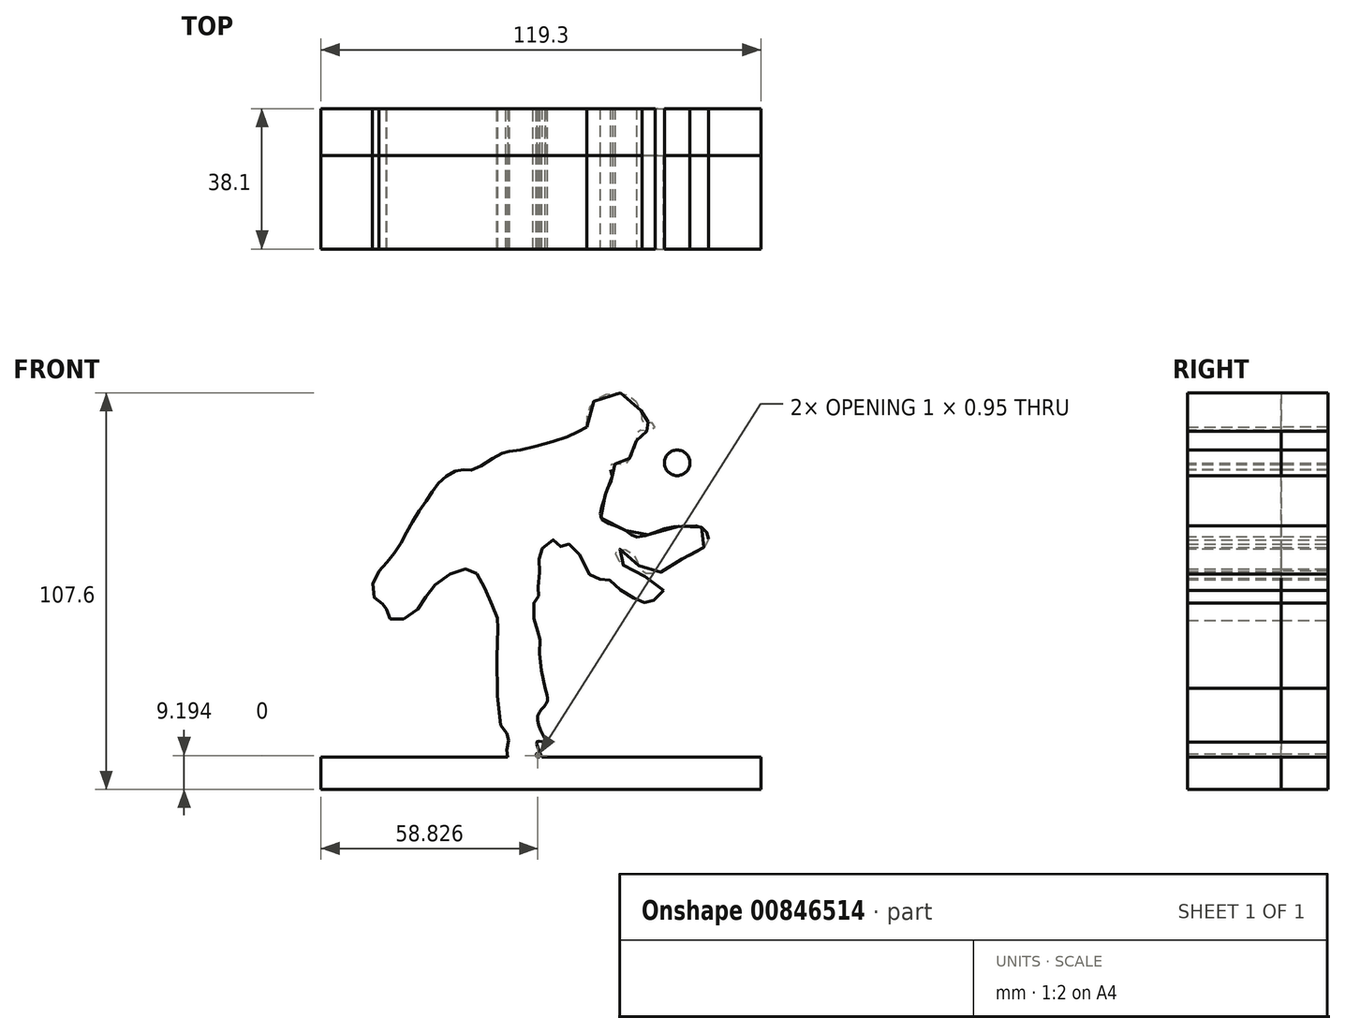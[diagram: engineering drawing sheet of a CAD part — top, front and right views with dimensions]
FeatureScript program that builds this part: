
annotation { "Feature Type Name" : "Feature", "Feature Type Description" : "" }
export const myFeature = defineFeature(function(context is Context, id is Id, definition is map)
    precondition{}
    {
        {
            var Q0;
            Q0=qCreatedBy(makeId("Front.planeOp"),FACE);
            var sketch = newSketch(context, id + "F0", { "sketchPlane" : qUnion([Q0])});
            skFitSpline(sketch, "E0", {"points": [v(-37.44, 0) * mm, v(-32.4, 6.14) * mm, v(-28.41, 13.3) * mm, v(-23.9, 20.2) * mm, v(-20.05, 25.12) * mm, v(-15.28, 27.5) * mm, v(-11.96, 27.5) * mm, v(-4.66, 31.75) * mm, v(-1.08, 32.55) * mm, v(12.46, 36) * mm, v(18.93, 39.1) * mm], "startDerivative": vector(50.52, 55.27) * mm, "endDerivative": vector(52.32, 30.3) * mm});
            skFitSpline(sketch, "E1", {"points": [v(18.93, 39.1) * mm, v(20.04, 45.09) * mm, v(25.4, 48.21) * mm, v(31.53, 46.87) * mm, v(33.88, 41.74) * mm, v(33.77, 40.62) * mm, v(37.11, 40.07) * mm, v(36.67, 38.06) * mm, v(32.87, 38.17) * mm, v(32.43, 36.05) * mm, v(31.65, 32.48) * mm, v(30.3, 30.25) * mm, v(29.08, 28.8) * mm, v(25.95, 29.13) * mm, v(25.28, 28.35) * mm, v(25.84, 25.34) * mm, v(24.62, 22.66) * mm, v(23.28, 18.2) * mm, v(22.83, 14.29) * mm, v(28.86, 11.39) * mm, v(32.43, 9.27) * mm, v(40.35, 11.61) * mm, v(46.38, 12.17) * mm, v(50.06, 11.83) * mm, v(51.93, 8.46) * mm, v(47.43, 4.33) * mm, v(44.05, 3.01) * mm, v(39.74, 0) * mm, v(33.73, 0) * mm, v(31.85, 4.33) * mm, v(26.79, 5.64) * mm, v(28.1, 2.26) * mm, v(31.85, 0) * mm, v(37.1, -3.18) * mm, v(39.74, -5.24) * mm, v(39.74, -4.5) * mm], "startDerivative": vector(2.53, 183.96) * mm, "endDerivative": vector(-15.3, 83.55) * mm});
            skFitSpline(sketch, "E2", {"points": [v(7.57, -31.72) * mm, v(6.15, -22.72) * mm, v(6.15, -17.52) * mm, v(5.2, -15.3) * mm, v(4.58, -8.52) * mm, v(5.84, -6.79) * mm, v(5.68, -4.84) * mm, v(6.15, 1.58) * mm, v(6.31, 5.2) * mm, v(10.1, 8.46) * mm, v(12.15, 6.47) * mm, v(14.83, 7.26) * mm, v(20.67, -2.05) * mm, v(23.83, -1.9) * mm, v(27.77, -4.84) * mm, v(33.3, -8.05) * mm, v(35.98, -8.52) * mm, v(39.74, -5.24) * mm], "startDerivative": vector(-24.18, 111.15) * mm, "endDerivative": vector(62.9, 70.23) * mm});
            skFitSpline(sketch, "E3", {"points": [v(-37.44, 0) * mm, v(-39.3, -4.84) * mm, v(-37.44, -8.68) * mm, v(-35.5, -9.15) * mm, v(-35.35, -11.68) * mm, v(-32.5, -13.41) * mm, v(-26.35, -9.63) * mm, v(-23.36, -4.84) * mm, v(-16.25, 0) * mm, v(-11.68, 0) * mm, v(-8.05, -6.47) * mm, v(-5.37, -12.62) * mm, v(-5.2, -15.47) * mm, v(-4.26, -42.45) * mm, v(-2.68, -44.03) * mm, v(-2.05, -44.98) * mm, v(-3, -48.3) * mm, v(-2.2, -48.92) * mm, v(-3, -52.7) * mm, v(1.26, -54.44) * mm, v(5.84, -53.34) * mm, v(5.2, -49.55) * mm, v(6.94, -51.29) * mm, v(5.37, -46.24) * mm, v(7.57, -46.4) * mm, v(5.52, -40.08) * mm, v(8.05, -35.67) * mm, v(7.57, -31.72) * mm], "startDerivative": vector(-70.2, -116.85) * mm, "endDerivative": vector(-43.82, 119.67) * mm});
            skCircle(sketch, "E4", {"center": v(43.42, 29.38) * mm, "radius": 3.46 * mm});
            skLineSegment(sketch, "E5.bottom", {"start": v(-53.18, -50.5) * mm, "end": v(66.12, -50.5) * mm});
            skLineSegment(sketch, "E5.top", {"start": v(-53.18, -59.22) * mm, "end": v(66.12, -59.22) * mm});
            skLineSegment(sketch, "E5.left", {"start": v(-53.18, -50.5) * mm, "end": v(-53.18, -59.22) * mm});
            skLineSegment(sketch, "E5.right", {"start": v(66.12, -50.5) * mm, "end": v(66.12, -59.22) * mm});
            skSolve(sketch);
        }
        {
            var Q0;
            Q0 = qSketchRegion(id + "F0", true);
            extrude(context, id + "F1", {"entities" : qUnion([Q0]), "oppositeDirection" : true, "depth" : 12.7 * mm, "offsetDistance" : 25.4 * mm});
        }
        {
            var Q0;
            Q0 = qSketchRegion(id + "F0", true);
            extrude(context, id + "F2", {"entities" : qUnion([Q0]), "depth" : 25.4 * mm, "offsetDistance" : 25.4 * mm});
        }
    });
